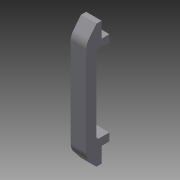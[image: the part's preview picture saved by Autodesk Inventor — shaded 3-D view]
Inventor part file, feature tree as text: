
AUTODESK INVENTOR PART (.ipt)
format: ipt  version: 2015 (Build 190159000, 159)  size: 103,424 bytes
history: native  units: in
note: dims shown in document units (in); Inventor stores cm internally (conversion verified against a paired STEP export)
features: extrude x1, fillet x1, sketch x1
ambient origin geometry x8: Origin, YZ Plane, XZ Plane, XY Plane, X Axis, Y Axis, Z Axis, Center Point
bodies: Solid1 (feature_tree)
feature tree (3):
  extrude  "Extrusion1"  Depth=1.1811in
  fillet  "Fillet1"  Radius=0.0787in
  sketch  "Sketch1"  dims[d1=0.1181in d4=1.1811in d5=0.0787in d7=0.1181in d10=0.2362in d11=0.0in d21=0.3937in d22=0.3937in d30=1.4961in d31=0.1575in d32=0.0787in d33=0.0787in d34=0.1969in d36=0.1181in d37=0.1181in d41=0.2362in d42=0.2362in]
